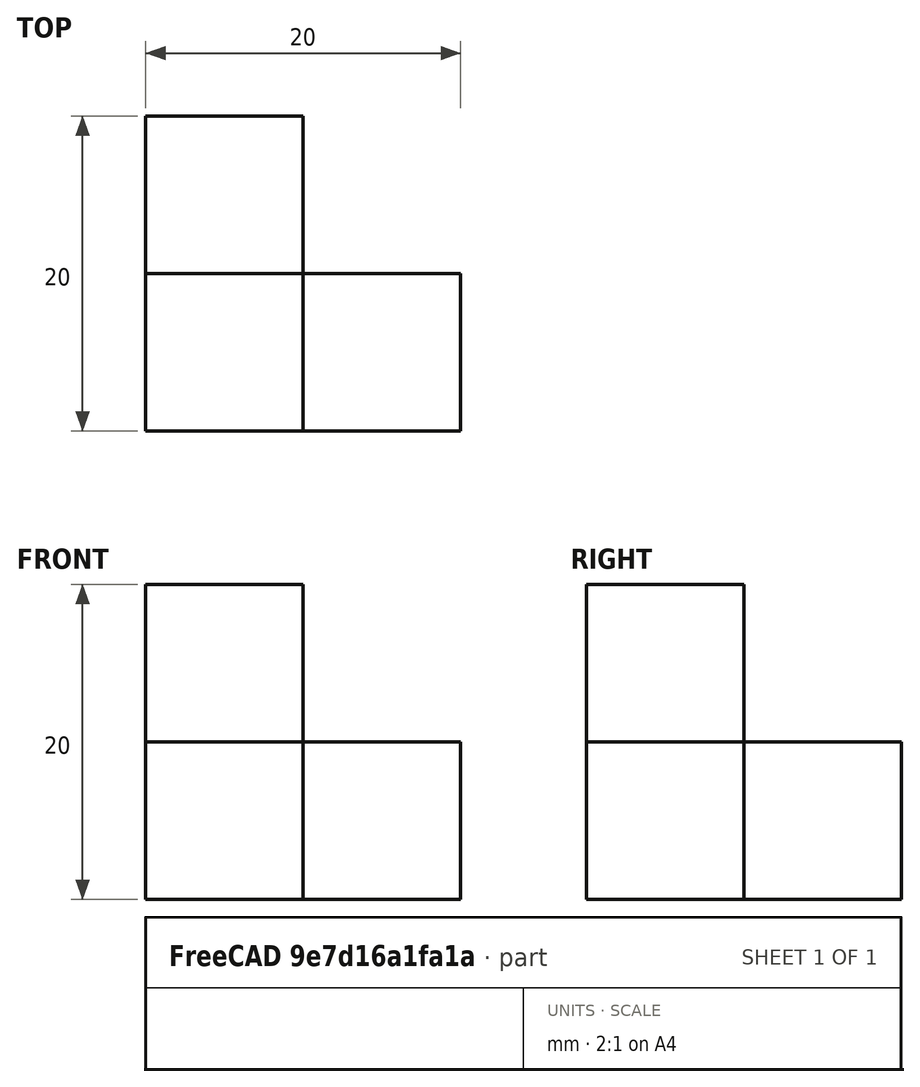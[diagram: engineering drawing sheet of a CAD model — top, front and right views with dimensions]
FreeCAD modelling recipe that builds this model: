
FCSTD DOCUMENT  (FreeCAD 1.0R39319 (Git))
Label: ojt1_t04p01_qbert 2 levels
License: All rights reserved
LicenseURL: https://en.wikipedia.org/wiki/All_rights_reserved
objects: Part::Box×4
note: 4 computed .brp shape members not serialized (recipe doc carries the construction recipe); baked Part::Feature solids carry a one-line shape summary decoded from their .brp

FEATURE [Part::Box] Box  label="Nivel1-cubo1"
  AttacherType = Attacher::AttachEngine3D
  Height = 10
  Length = 10
  Width = 10
FEATURE [Part::Box] Box001  label="Nivel2-cubo1"
  AttacherType = Attacher::AttachEngine3D
  Height = 10
  Length = 10
  Placement = pos=(10,0,0) rot=(0,0,1;0rad)
  Width = 10
FEATURE [Part::Box] Box002  label="Nivel2-cubo2"
  AttacherType = Attacher::AttachEngine3D
  Height = 10
  Length = 10
  Placement = pos=(0,10,0) rot=(0,0,1;0rad)
  Width = 10
FEATURE [Part::Box] Box003  label="Cub"
  AttacherType = Attacher::AttachEngine3D
  Height = 10
  Length = 10
  Placement = pos=(0,0,10) rot=(0,0,1;0rad)
  Width = 10
